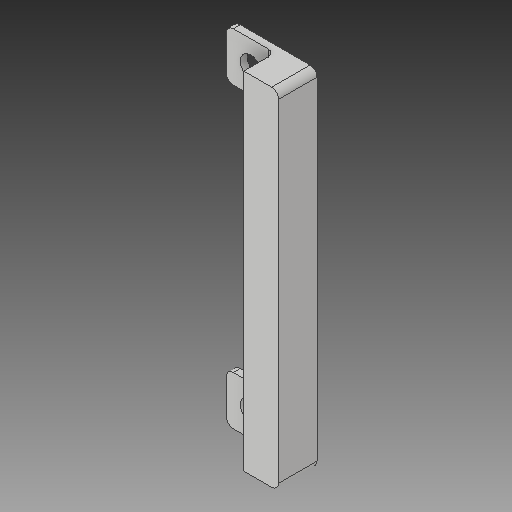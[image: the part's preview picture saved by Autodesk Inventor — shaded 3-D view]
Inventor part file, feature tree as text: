
AUTODESK INVENTOR PART (.ipt)
format: ipt  version: 2018 (Build 220112000, 112)  size: 157,696 bytes
history: native  units: mm
features: reference x6, other x5, fillet x3, sketch x2, plane x2, extrude x2
ambient origin geometry x8: Origin, YZ Plane, XZ Plane, XY Plane, X Axis, Y Axis, Z Axis, Center Point
bodies: Solid1 (feature_tree)
feature tree (20):
  sketch  "Sketch1"  dims[d0=0.5mm d1=5.0mm]
  plane  "Work Plane1"
  extrude  "Extrusion1"  Depth=5.0mm
  plane  "Work Plane2"
  extrude  "Extrusion2"  Depth=7.0mm
  fillet  "Fillet1"  Radius=7.0mm
  fillet  "Fillet2"  Radius=3.0mm
  fillet  "Fillet3"  Radius=2.0mm
  reference  "Reference1"
  reference  "Reference2"
  reference  "Reference3"
  sketch  "Sketch2"  dims[d2=10.0mm d3=0.0mm d4=7.0mm d5=7.0mm d6=3.0mm d7=2.0mm d8=0.0mm d9=1.0mm d10=1.0mm d11=1.0mm]
  reference  "Reference4"
  reference  "Reference5"
  reference  "Reference6"
  other  "<userpath>\OneDrive\Documents\Inventor\TSA\2018\Animatronics\Tortoise\Turtle3.iam"
  other  "Turtle3.iam"
  other  "HeadOpenRack:2"
  other  "SyringeMotorBase_MIR:1"
  other  "Supporter:1"
